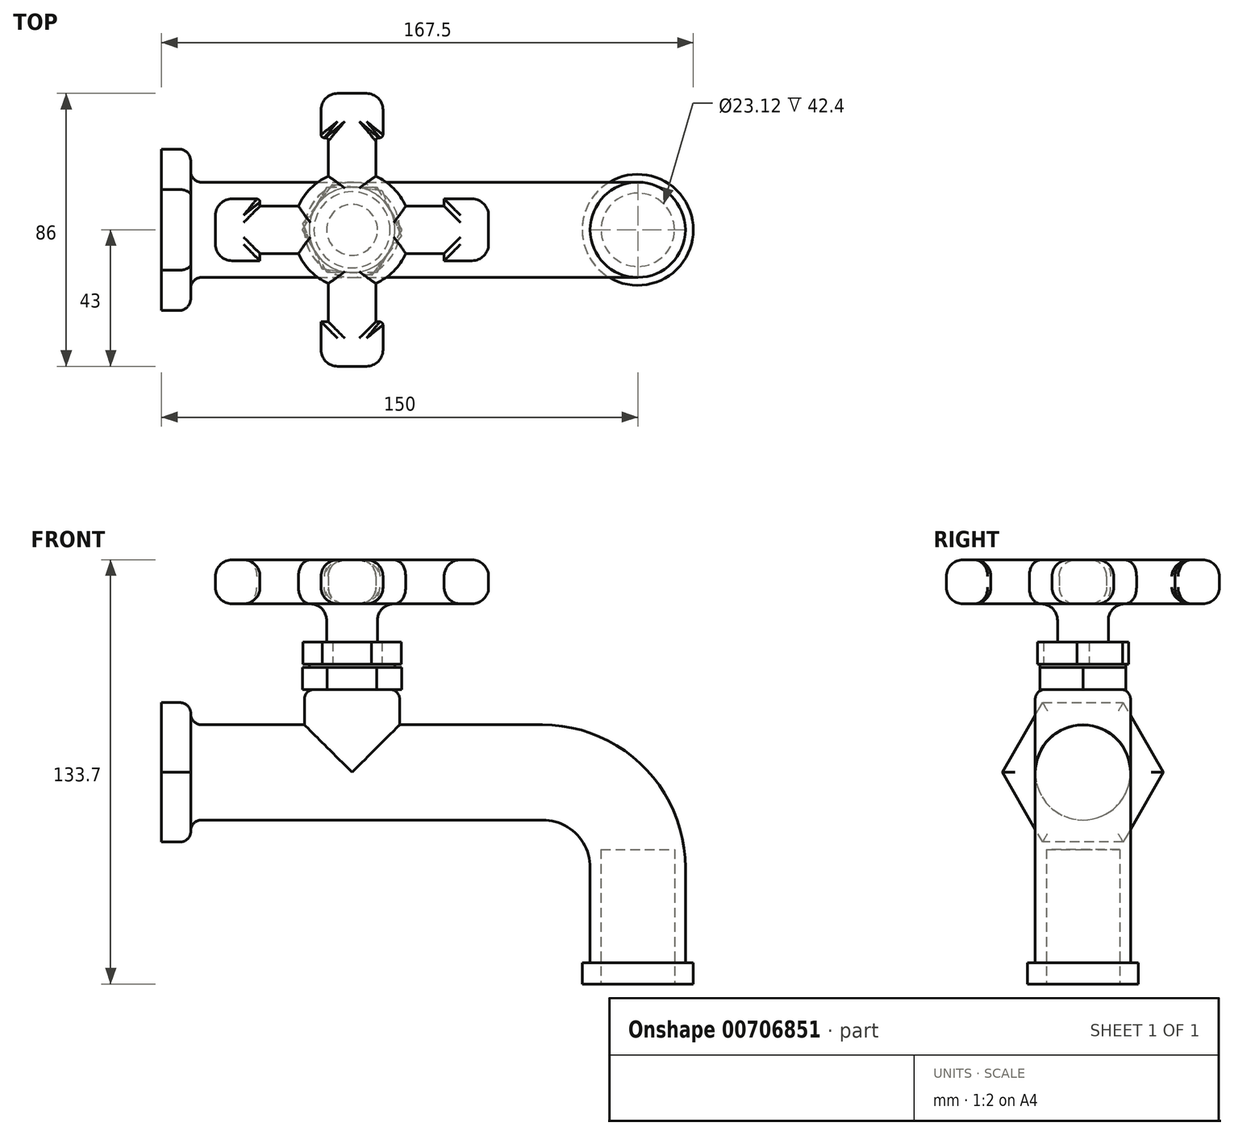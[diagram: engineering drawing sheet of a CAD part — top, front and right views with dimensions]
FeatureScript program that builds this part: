
annotation { "Feature Type Name" : "Feature", "Feature Type Description" : "" }
export const myFeature = defineFeature(function(context is Context, id is Id, definition is map)
    precondition{}
    {
        {
            var Q0;
            Q0=qCreatedBy(makeId("Front.planeOp"),FACE);
            var sketch = newSketch(context, id + "F0", { "sketchPlane" : qUnion([Q0])});
            skLineSegment(sketch, "E0", {"start": v(-60, 0) * mm, "end": v(60, 0) * mm});
            skLineSegment(sketch, "E1", {"start": v(90, -30) * mm, "end": v(90, -60) * mm});
            skPoint(sketch, "E2.visualSharp", {"position": v(90, 0) * mm});
            skArc(sketch, "E2.filletArc", {"start": v(90, -30) * mm, "mid": v(81.21, -8.79) * mm, "end": v(60, 0) * mm});
            skSolve(sketch);
        }
        {
            var Q0;
            Q0=sQuery(id+"F0.wireOp",VERTEX,"E0.start");
            var Q1;
            Q1=qCreatedBy(makeId("Right.planeOp"),FACE);
            cPlane(context, id + "F1", {"entities" : qUnion([Q0, Q1]), "cplaneType" : CPlaneType.PLANE_POINT, "offset" : 25 * mm, "width" : 150 * mm, "height" : 150 * mm});
        }
        {
            var Q0;
            Q0=qCreatedBy(id+"F1.planeOp",FACE);
            var sketch = newSketch(context, id + "F2", { "sketchPlane" : qUnion([Q0])});
            skCircle(sketch, "E3", {"center": v(0, 0) * mm, "radius": 15 * mm});
            skSolve(sketch);
        }
        {
            var Q0;
            Q0=makeQuery(id+"F2.imprint","IMPRINT",FACE,{"disambiguationData":[TD([[makeQuery(id+"F2.imprint","IMPRINT",EDGE,{"derivedFrom":sQuery(id+"F2.wireOp",EDGE,"E3")}),1.0]])]});
            var Q1;
            Q1=sQuery(id+"F0.wireOp",EDGE,"E0");
            var Q2;
            Q2=sQuery(id+"F0.wireOp",EDGE,"E2.filletArc");
            var Q3;
            Q3=sQuery(id+"F0.wireOp",EDGE,"E1");
            sweep(context, id + "F3", {"profiles" : qUnion([Q0]), "path" : qUnion([Q1, Q2, Q3])});
        }
        {
            var Q0;
            Q0=qCreatedBy(makeId("Top.planeOp"),FACE);
            var sketch = newSketch(context, id + "F4", { "sketchPlane" : qUnion([Q0])});
            skLineSegment(sketch, "E4.0", {"start": v(-60, 0) * mm, "end": v(60, 0) * mm, "construction": true});
            skCircle(sketch, "E5", {"center": v(0, 0) * mm, "radius": 15 * mm});
            skSolve(sketch);
        }
        {
            var Q0;
            Q0=qSketchRegion(id+"F4",true);
            extrude(context, id + "F5", {"entities" : qUnion([Q0]), "operationType" : NewBodyOperationType.ADD, "depth" : 26.1 * mm});
        }
        {
            var Q0;
            Q0=makeQuery(id+"F5.opExtrude","CAP_FACE",FACE,{"disambiguationData":[OSD([sQuery(id+"F4.wireOp",EDGE,"E5")])],"isStart":false});
            fillet(context, id + "F6", {"entities" : qUnion([Q0]), "radius" : 3 * mm, "tangentPropagation" : true, "allowEdgeOverflow" : false});
        }
        {
            var Q0;
            Q0=makeQuery(id+"F5.opExtrude","CAP_FACE",FACE,{"disambiguationData":[OSD([sQuery(id+"F4.wireOp",EDGE,"E5")])],"isStart":false});
            var sketch = newSketch(context, id + "F7", { "sketchPlane" : qUnion([Q0])});
            skCircle(sketch, "E6.cCircle", {"center": v(0, 0) * mm, "radius": 13.5 * mm, "construction": true});
            skLineSegment(sketch, "E6.0", {"start": v(15.59, 0) * mm, "end": v(7.8, -13.5) * mm});
            skLineSegment(sketch, "E6.1", {"start": v(7.8, -13.5) * mm, "end": v(-7.8, -13.5) * mm});
            skLineSegment(sketch, "E6.2", {"start": v(-7.8, -13.5) * mm, "end": v(-15.59, 0) * mm});
            skLineSegment(sketch, "E6.3", {"start": v(-15.59, 0) * mm, "end": v(-7.8, 13.5) * mm});
            skLineSegment(sketch, "E6.4", {"start": v(-7.8, 13.5) * mm, "end": v(7.8, 13.5) * mm});
            skLineSegment(sketch, "E6.5", {"start": v(7.8, 13.5) * mm, "end": v(15.59, 0) * mm});
            skPoint(sketch, "E6.0.midPoint", {"position": v(11.7, -6.75) * mm});
            skSolve(sketch);
        }
        {
            var Q0;
            Q0=qSketchRegion(id+"F7",true);
            extrude(context, id + "F8", {"entities" : qUnion([Q0]), "operationType" : NewBodyOperationType.ADD, "depth" : 7 * mm});
        }
        {
            var Q0;
            Q0=makeQuery(id+"F8.opExtrude","CAP_FACE",FACE,{"disambiguationData":[OSD([sQuery(id+"F7.wireOp",EDGE,"E6.0"),sQuery(id+"F7.wireOp",EDGE,"E6.1"),sQuery(id+"F7.wireOp",EDGE,"E6.2"),sQuery(id+"F7.wireOp",EDGE,"E6.3"),sQuery(id+"F7.wireOp",EDGE,"E6.4"),sQuery(id+"F7.wireOp",EDGE,"E6.5")])],"isStart":false});
            var sketch = newSketch(context, id + "F9", { "sketchPlane" : qUnion([Q0])});
            skCircle(sketch, "E7.0", {"center": v(0, 0) * mm, "radius": 13.5 * mm});
            skSolve(sketch);
        }
        {
            var Q0;
            Q0=qSketchRegion(id+"F9",true);
            extrude(context, id + "F10", {"entities" : qUnion([Q0]), "operationType" : NewBodyOperationType.ADD, "depth" : 1 * mm});
        }
        {
            var Q0;
            Q0=makeQuery(id+"F10.opExtrude","CAP_FACE",FACE,{"disambiguationData":[OSD([sQuery(id+"F9.wireOp",EDGE,"E7.0")])],"isStart":false});
            var sketch = newSketch(context, id + "F11", { "sketchPlane" : qUnion([Q0])});
            skCircle(sketch, "E8.cCircle", {"center": v(0, 0) * mm, "radius": 13.5 * mm, "construction": true});
            skLineSegment(sketch, "E8.0", {"start": v(9.38, 12.45) * mm, "end": v(15.47, -1.9) * mm});
            skLineSegment(sketch, "E8.1", {"start": v(15.47, -1.9) * mm, "end": v(6.1, -14.35) * mm});
            skLineSegment(sketch, "E8.2", {"start": v(6.1, -14.35) * mm, "end": v(-9.38, -12.45) * mm});
            skLineSegment(sketch, "E8.3", {"start": v(-9.38, -12.45) * mm, "end": v(-15.47, 1.9) * mm});
            skLineSegment(sketch, "E8.4", {"start": v(-15.47, 1.9) * mm, "end": v(-6.1, 14.35) * mm});
            skLineSegment(sketch, "E8.5", {"start": v(-6.1, 14.35) * mm, "end": v(9.38, 12.45) * mm});
            skPoint(sketch, "E8.0.midPoint", {"position": v(12.42, 5.28) * mm});
            skSolve(sketch);
        }
        {
            var Q0;
            Q0=qSketchRegion(id+"F11",true);
            extrude(context, id + "F12", {"entities" : qUnion([Q0]), "operationType" : NewBodyOperationType.ADD, "depth" : 7 * mm});
        }
        {
            var Q0;
            Q0=makeQuery(id+"F12.opExtrude","CAP_FACE",FACE,{"disambiguationData":[OSD([sQuery(id+"F11.wireOp",EDGE,"E8.0"),sQuery(id+"F11.wireOp",EDGE,"E8.1"),sQuery(id+"F11.wireOp",EDGE,"E8.2"),sQuery(id+"F11.wireOp",EDGE,"E8.3"),sQuery(id+"F11.wireOp",EDGE,"E8.4"),sQuery(id+"F11.wireOp",EDGE,"E8.5")])],"isStart":false});
            var sketch = newSketch(context, id + "F13", { "sketchPlane" : qUnion([Q0])});
            skCircle(sketch, "E9", {"center": v(0, 0) * mm, "radius": 8 * mm});
            skSolve(sketch);
        }
        {
            var Q0;
            Q0=qSketchRegion(id+"F13",true);
            extrude(context, id + "F14", {"entities" : qUnion([Q0]), "operationType" : NewBodyOperationType.ADD, "depth" : 12 * mm});
        }
        {
            var Q0;
            Q0=makeQuery(id+"F14.opExtrude","CAP_FACE",FACE,{"disambiguationData":[OSD([sQuery(id+"F13.wireOp",EDGE,"E9")])],"isStart":false});
            var sketch = newSketch(context, id + "F15", { "sketchPlane" : qUnion([Q0])});
            skPoint(sketch, "E10.middle", {"position": v(0, 0) * mm});
            skLineSegment(sketch, "E11.bottom", {"start": v(-29, 7.47) * mm, "end": v(-16.88, 7.47) * mm});
            skLineSegment(sketch, "E11.top", {"start": v(-29, -7.47) * mm, "end": v(-16.88, -7.47) * mm});
            skLineSegment(sketch, "E12.left", {"start": v(-43, 9.74) * mm, "end": v(-43, -9.74) * mm});
            skLineSegment(sketch, "E12.right", {"start": v(-29, 9.74) * mm, "end": v(-29, 7.47) * mm});
            skLineSegment(sketch, "E13.left", {"start": v(43, 9.74) * mm, "end": v(43, -9.74) * mm});
            skLineSegment(sketch, "E13.right", {"start": v(29, 9.74) * mm, "end": v(29, 7.47) * mm});
            skArc(sketch, "E14", {"start": v(-16.88, -7.47) * mm, "mid": v(-13.05, -13.05) * mm, "end": v(-7.47, -16.88) * mm});
            skLineSegment(sketch, "E15.trimOffspring", {"start": v(16.88, 7.47) * mm, "end": v(29, 7.47) * mm});
            skLineSegment(sketch, "E16.trimOffspring", {"start": v(16.88, -7.47) * mm, "end": v(29, -7.47) * mm});
            skArc(sketch, "E17.trimOffspring", {"start": v(16.88, 7.47) * mm, "mid": v(13.05, 13.05) * mm, "end": v(7.47, 16.88) * mm});
            skLineSegment(sketch, "E18.trimOffspring", {"start": v(-29, -7.47) * mm, "end": v(-29, -9.74) * mm});
            skLineSegment(sketch, "E19.1.0", {"start": v(-7.47, -16.88) * mm, "end": v(-7.47, -29) * mm});
            skLineSegment(sketch, "E19.1.1", {"start": v(7.47, -16.88) * mm, "end": v(7.47, -29) * mm});
            skLineSegment(sketch, "E19.1.2", {"start": v(9.74, 43) * mm, "end": v(-9.74, 43) * mm});
            skLineSegment(sketch, "E19.1.4", {"start": v(9.74, -29) * mm, "end": v(7.47, -29) * mm});
            skArc(sketch, "E19.1.5", {"start": v(-7.47, 16.88) * mm, "mid": v(-13.05, 13.05) * mm, "end": v(-16.88, 7.47) * mm});
            skLineSegment(sketch, "E19.1.7", {"start": v(9.74, 29) * mm, "end": v(7.47, 29) * mm});
            skLineSegment(sketch, "E19.1.9", {"start": v(-7.47, 29) * mm, "end": v(-9.74, 29) * mm});
            skLineSegment(sketch, "E19.1.10", {"start": v(-7.47, 29) * mm, "end": v(-7.47, 16.88) * mm});
            skLineSegment(sketch, "E19.1.11", {"start": v(7.47, 29) * mm, "end": v(7.47, 16.88) * mm});
            skArc(sketch, "E19.1.18", {"start": v(7.47, -16.88) * mm, "mid": v(13.05, -13.05) * mm, "end": v(16.88, -7.47) * mm});
            skLineSegment(sketch, "E19.1.19", {"start": v(9.74, -43) * mm, "end": v(-9.74, -43) * mm});
            skLineSegment(sketch, "E19.1.20", {"start": v(-7.27, -29) * mm, "end": v(-9.74, -29) * mm});
            skLineSegment(sketch, "E19.1.23", {"start": v(-9.74, -29) * mm, "end": v(-7.27, -29) * mm});
            skLineSegment(sketch, "E19.anchor1", {"start": v(0, 0) * mm, "end": v(-43, -13) * mm, "construction": true});
            skLineSegment(sketch, "E19.anchor2", {"start": v(0, 0) * mm, "end": v(-13, 43) * mm, "construction": true});
            skLineSegment(sketch, "E20", {"start": v(29, -7.47) * mm, "end": v(29, -9.74) * mm});
            skLineSegment(sketch, "E21.bottom", {"start": v(43, 9.74) * mm, "end": v(29, 9.74) * mm});
            skLineSegment(sketch, "E21.top", {"start": v(43, -9.74) * mm, "end": v(29, -9.74) * mm});
            skLineSegment(sketch, "E22.trimOffspring", {"start": v(-29, 9.74) * mm, "end": v(-43, 9.74) * mm});
            skLineSegment(sketch, "E23.trimOffspring", {"start": v(-29, -9.74) * mm, "end": v(-43, -9.74) * mm});
            skLineSegment(sketch, "E24.left", {"start": v(9.74, 43) * mm, "end": v(9.74, 29) * mm});
            skLineSegment(sketch, "E24.right", {"start": v(-9.74, 43) * mm, "end": v(-9.74, 29) * mm});
            skLineSegment(sketch, "E25.trimOffspring", {"start": v(-9.74, -29) * mm, "end": v(-9.74, -43) * mm});
            skLineSegment(sketch, "E26.trimOffspring", {"start": v(9.74, -29) * mm, "end": v(9.74, -43) * mm});
            skSolve(sketch);
        }
        {
            var Q0;
            Q0=qSketchRegion(id+"F15",true);
            extrude(context, id + "F16", {"entities" : qUnion([Q0]), "operationType" : NewBodyOperationType.ADD, "depth" : 13.9 * mm});
        }
        {
            var Q0;
            Q0=makeQuery(id+"F16.opExtrude","CAP_FACE",FACE,{"disambiguationData":[OSD([sQuery(id+"F15.wireOp",EDGE,"E11.bottom"),sQuery(id+"F15.wireOp",EDGE,"E11.top"),sQuery(id+"F15.wireOp",EDGE,"E12.right"),sQuery(id+"F15.wireOp",EDGE,"E13.right"),sQuery(id+"F15.wireOp",EDGE,"E15.trimOffspring"),sQuery(id+"F15.wireOp",EDGE,"E16.trimOffspring"),sQuery(id+"F15.wireOp",EDGE,"E18.trimOffspring"),sQuery(id+"F15.wireOp",EDGE,"E19.1.0"),sQuery(id+"F15.wireOp",EDGE,"E19.1.1"),sQuery(id+"F15.wireOp",EDGE,"E19.1.2"),sQuery(id+"F15.wireOp",EDGE,"E19.1.4"),sQuery(id+"F15.wireOp",EDGE,"E19.1.7"),sQuery(id+"F15.wireOp",EDGE,"E19.1.9"),sQuery(id+"F15.wireOp",EDGE,"E19.1.10"),sQuery(id+"F15.wireOp",EDGE,"E19.1.11"),sQuery(id+"F15.wireOp",EDGE,"E19.1.19"),sQuery(id+"F15.wireOp",EDGE,"E19.1.23"),sQuery(id+"F15.wireOp",EDGE,"E19.1.5"),sQuery(id+"F15.wireOp",EDGE,"E17.trimOffspring"),sQuery(id+"F15.wireOp",EDGE,"E19.1.18"),sQuery(id+"F15.wireOp",EDGE,"E14"),sQuery(id+"F15.wireOp",EDGE,"E20"),sQuery(id+"F15.wireOp",EDGE,"E21.bottom"),sQuery(id+"F15.wireOp",EDGE,"E21.top"),sQuery(id+"F15.wireOp",EDGE,"E13.left"),sQuery(id+"F15.wireOp",EDGE,"E12.left"),sQuery(id+"F15.wireOp",EDGE,"E22.trimOffspring"),sQuery(id+"F15.wireOp",EDGE,"E23.trimOffspring"),sQuery(id+"F15.wireOp",EDGE,"E24.left"),sQuery(id+"F15.wireOp",EDGE,"E24.right"),sQuery(id+"F15.wireOp",EDGE,"E25.trimOffspring"),sQuery(id+"F15.wireOp",EDGE,"E26.trimOffspring")])],"isStart":true});
            var Q1;
            Q1=makeQuery(id+"F16.opExtrude","CAP_FACE",FACE,{"disambiguationData":[OSD([sQuery(id+"F15.wireOp",EDGE,"E11.bottom"),sQuery(id+"F15.wireOp",EDGE,"E11.top"),sQuery(id+"F15.wireOp",EDGE,"E12.right"),sQuery(id+"F15.wireOp",EDGE,"E13.right"),sQuery(id+"F15.wireOp",EDGE,"E15.trimOffspring"),sQuery(id+"F15.wireOp",EDGE,"E16.trimOffspring"),sQuery(id+"F15.wireOp",EDGE,"E18.trimOffspring"),sQuery(id+"F15.wireOp",EDGE,"E19.1.0"),sQuery(id+"F15.wireOp",EDGE,"E19.1.1"),sQuery(id+"F15.wireOp",EDGE,"E19.1.2"),sQuery(id+"F15.wireOp",EDGE,"E19.1.4"),sQuery(id+"F15.wireOp",EDGE,"E19.1.7"),sQuery(id+"F15.wireOp",EDGE,"E19.1.9"),sQuery(id+"F15.wireOp",EDGE,"E19.1.10"),sQuery(id+"F15.wireOp",EDGE,"E19.1.11"),sQuery(id+"F15.wireOp",EDGE,"E19.1.19"),sQuery(id+"F15.wireOp",EDGE,"E19.1.23"),sQuery(id+"F15.wireOp",EDGE,"E19.1.5"),sQuery(id+"F15.wireOp",EDGE,"E17.trimOffspring"),sQuery(id+"F15.wireOp",EDGE,"E19.1.18"),sQuery(id+"F15.wireOp",EDGE,"E14"),sQuery(id+"F15.wireOp",EDGE,"E20"),sQuery(id+"F15.wireOp",EDGE,"E21.bottom"),sQuery(id+"F15.wireOp",EDGE,"E21.top"),sQuery(id+"F15.wireOp",EDGE,"E13.left"),sQuery(id+"F15.wireOp",EDGE,"E12.left"),sQuery(id+"F15.wireOp",EDGE,"E22.trimOffspring"),sQuery(id+"F15.wireOp",EDGE,"E23.trimOffspring"),sQuery(id+"F15.wireOp",EDGE,"E24.left"),sQuery(id+"F15.wireOp",EDGE,"E24.right"),sQuery(id+"F15.wireOp",EDGE,"E25.trimOffspring"),sQuery(id+"F15.wireOp",EDGE,"E26.trimOffspring")])],"isStart":false});
            var Q2;
            Q2=makeQuery(id+"F16.opExtrude","SWEPT_FACE",FACE,{"disambiguationData":[OSD([sQuery(id+"F15.wireOp",EDGE,"E19.1.19")])]});
            var Q3;
            Q3=makeQuery(id+"F16.opExtrude","SWEPT_FACE",FACE,{"disambiguationData":[OSD([sQuery(id+"F15.wireOp",EDGE,"E12.left")])]});
            var Q4;
            Q4=makeQuery(id+"F16.opExtrude","SWEPT_FACE",FACE,{"disambiguationData":[OSD([sQuery(id+"F15.wireOp",EDGE,"E19.1.2")])]});
            var Q5;
            Q5=makeQuery(id+"F16.opExtrude","SWEPT_FACE",FACE,{"disambiguationData":[OSD([sQuery(id+"F15.wireOp",EDGE,"E13.left")])]});
            fillet(context, id + "F17", {"entities" : qUnion([Q0, Q1, Q2, Q3, Q4, Q5]), "radius" : 5.2 * mm, "tangentPropagation" : true, "allowEdgeOverflow" : false});
        }
        {
            var Q0;
            {var subQ0=sQuery(id+"F15.wireOp",EDGE,"E22.trimOffspring");Q0=makeQuery(id+"F17.opFillet","BLEND_FACE",FACE,{"disambiguationData":[OSD([subQ0]),TDD([makeQuery(id+"F16.opExtrude","CAP_EDGE",EDGE,{"disambiguationData":[OSD([subQ0])],"isStart":false})])]});}
            var Q1;
            {var subQ0=sQuery(id+"F15.wireOp",EDGE,"E26.trimOffspring");Q1=makeQuery(id+"F17.opFillet","BLEND_FACE",FACE,{"disambiguationData":[OSD([subQ0]),TDD([makeQuery(id+"F16.opExtrude","CAP_EDGE",EDGE,{"disambiguationData":[OSD([subQ0])],"isStart":false})])]});}
            var Q2;
            Q2=makeQuery(id+"F16.opExtrude","SWEPT_FACE",FACE,{"disambiguationData":[OSD([sQuery(id+"F15.wireOp",EDGE,"E19.1.7")])]});
            var Q3;
            {var subQ0=sQuery(id+"F15.wireOp",EDGE,"E19.1.9");Q3=makeQuery(id+"F17.opFillet","BLEND_FACE",FACE,{"disambiguationData":[OSD([subQ0]),TDD([makeQuery(id+"F16.opExtrude","CAP_EDGE",EDGE,{"disambiguationData":[OSD([subQ0])],"isStart":true})])]});}
            var Q4;
            {var subQ0=sQuery(id+"F15.wireOp",EDGE,"E19.1.9");Q4=makeQuery(id+"F17.opFillet","BLEND_FACE",FACE,{"disambiguationData":[OSD([subQ0]),TDD([makeQuery(id+"F16.opExtrude","CAP_EDGE",EDGE,{"disambiguationData":[OSD([subQ0])],"isStart":false})])]});}
            fillet(context, id + "F18", {"entities" : qUnion([Q0, Q1, Q2, Q3, Q4]), "radius" : 1 * mm, "tangentPropagation" : true, "allowEdgeOverflow" : false});
        }
        {
            var Q0;
            Q0=makeQuery(id+"F2.imprint","IMPRINT",FACE,{"disambiguationData":[TD([[makeQuery(id+"F2.imprint","IMPRINT",EDGE,{"derivedFrom":sQuery(id+"F2.wireOp",EDGE,"E3")}),1.0]])]});
            var sketch = newSketch(context, id + "F19", { "sketchPlane" : qUnion([Q0])});
            skCircle(sketch, "E27.cCircle", {"center": v(0, 0) * mm, "radius": 21.98 * mm, "construction": true});
            skLineSegment(sketch, "E27.0", {"start": v(-12.69, -21.98) * mm, "end": v(-25.38, 0) * mm});
            skLineSegment(sketch, "E27.1", {"start": v(-25.38, 0) * mm, "end": v(-12.69, 21.98) * mm});
            skLineSegment(sketch, "E27.2", {"start": v(-12.69, 21.98) * mm, "end": v(12.69, 21.98) * mm});
            skLineSegment(sketch, "E27.3", {"start": v(12.69, 21.98) * mm, "end": v(25.38, 0) * mm});
            skLineSegment(sketch, "E27.4", {"start": v(25.38, 0) * mm, "end": v(12.69, -21.98) * mm});
            skLineSegment(sketch, "E27.5", {"start": v(12.69, -21.98) * mm, "end": v(-12.69, -21.98) * mm});
            skPoint(sketch, "E27.0.midPoint", {"position": v(-19.03, -10.99) * mm});
            skSolve(sketch);
        }
        {
            var Q0;
            Q0=qSketchRegion(id+"F19",true);
            extrude(context, id + "F20", {"entities" : qUnion([Q0]), "operationType" : NewBodyOperationType.ADD, "depth" : 9.2 * mm});
        }
        {
            var Q0;
            Q0=makeQuery(id+"F20.opExtrude","CAP_FACE",FACE,{"disambiguationData":[OSD([sQuery(id+"F19.wireOp",EDGE,"E27.0"),sQuery(id+"F19.wireOp",EDGE,"E27.1"),sQuery(id+"F19.wireOp",EDGE,"E27.2"),sQuery(id+"F19.wireOp",EDGE,"E27.3"),sQuery(id+"F19.wireOp",EDGE,"E27.4"),sQuery(id+"F19.wireOp",EDGE,"E27.5")])],"isStart":false});
            fillet(context, id + "F21", {"entities" : qUnion([Q0]), "radius" : 3.4 * mm, "tangentPropagation" : true, "allowEdgeOverflow" : false});
        }
        {
            var Q0;
            Q0=makeQuery(id+"F3.opSweep","CAP_FACE",FACE,{"disambiguationData":[OSD([sQuery(id+"F0.wireOp",VERTEX,"E1.end"),sQuery(id+"F2.wireOp",EDGE,"E3")])],"isStart":false});
            var sketch = newSketch(context, id + "F22", { "sketchPlane" : qUnion([Q0])});
            skCircle(sketch, "E28", {"center": v(90, 0) * mm, "radius": 17.5 * mm});
            skSolve(sketch);
        }
        {
            var Q0;
            Q0=qSketchRegion(id+"F22",true);
            extrude(context, id + "F23", {"entities" : qUnion([Q0]), "operationType" : NewBodyOperationType.ADD, "depth" : 6.7 * mm});
        }
        {
            var Q0;
            Q0=makeQuery(id+"F23.opExtrude","CAP_FACE",FACE,{"disambiguationData":[OSD([sQuery(id+"F22.wireOp",EDGE,"E28")])],"isStart":false});
            var sketch = newSketch(context, id + "F24", { "sketchPlane" : qUnion([Q0])});
            skCircle(sketch, "E29", {"center": v(90, 0) * mm, "radius": 11.56 * mm});
            skSolve(sketch);
        }
        {
            var Q0;
            Q0=qSketchRegion(id+"F24",true);
            extrude(context, id + "F25", {"entities" : qUnion([Q0]), "operationType" : NewBodyOperationType.REMOVE, "oppositeDirection" : true, "depth" : 42.4 * mm});
        }
    });
